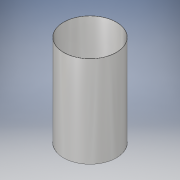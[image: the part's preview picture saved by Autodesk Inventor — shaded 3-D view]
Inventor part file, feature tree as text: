
AUTODESK INVENTOR PART (.ipt)
format: ipt  version: 2018 (Build 220112000, 112)  size: 103,936 bytes
history: native  units: in
note: dims shown in document units (in); Inventor stores cm internally (conversion verified against a paired STEP export)
features: extrude x1, sketch x1
ambient origin geometry x8: Origin, YZ Plane, XZ Plane, XY Plane, X Axis, Y Axis, Z Axis, Center Point
bodies: Solid1 (feature_tree)
feature tree (2):
  extrude  "Extrusion1"  Depth=19.0in
  sketch  "Sketch1"  dims[d0=10.9in d1=11.0in d2=19.0in d3=0.0in]
